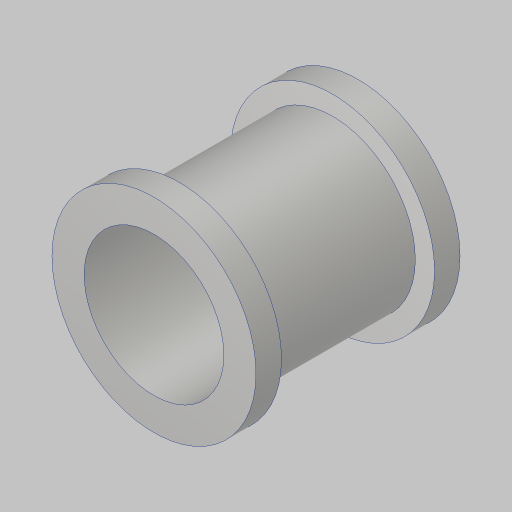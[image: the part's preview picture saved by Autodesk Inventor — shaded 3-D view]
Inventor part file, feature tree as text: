
AUTODESK INVENTOR PART (.ipt)
format: ipt  version: 2023.5 (Build 275446000, 446)  size: 150,528 bytes
history: native  units: in
note: dims shown in document units (in); Inventor stores cm internally (conversion verified against a paired STEP export)
features: extrude x3, sketch x3, projected_geometry x2
ambient origin geometry x8: Origin, YZ Plane, XZ Plane, XY Plane, X Axis, Y Axis, Z Axis, Center Point
bodies: Solid1 (feature_tree)
feature tree (8):
  extrude  "Extrusion1"  Depth=1.0in
  extrude  "Extrusion2"  Depth=1.0in
  extrude  "Extrusion3"  Depth=1.0in
  sketch  "Sketch1"  dims[d1=1.0in d2=6.0in]
  sketch  "Sketch2"  dims[d3=1.0in d4=6.0in]
  projected_geometry  "Projected Loop1"
  sketch  "Sketch3"  dims[d5=0.25in d6=0.685in d7=0.0625in d8=0.015in d11=0.812in d12=0.75in d13=0.0in d15=0.125in d16=0.0in d18=0.125in d19=0.0in d21=0.391in d22=1.0in d23=1.0in]
  projected_geometry  "Projected Loop2"
